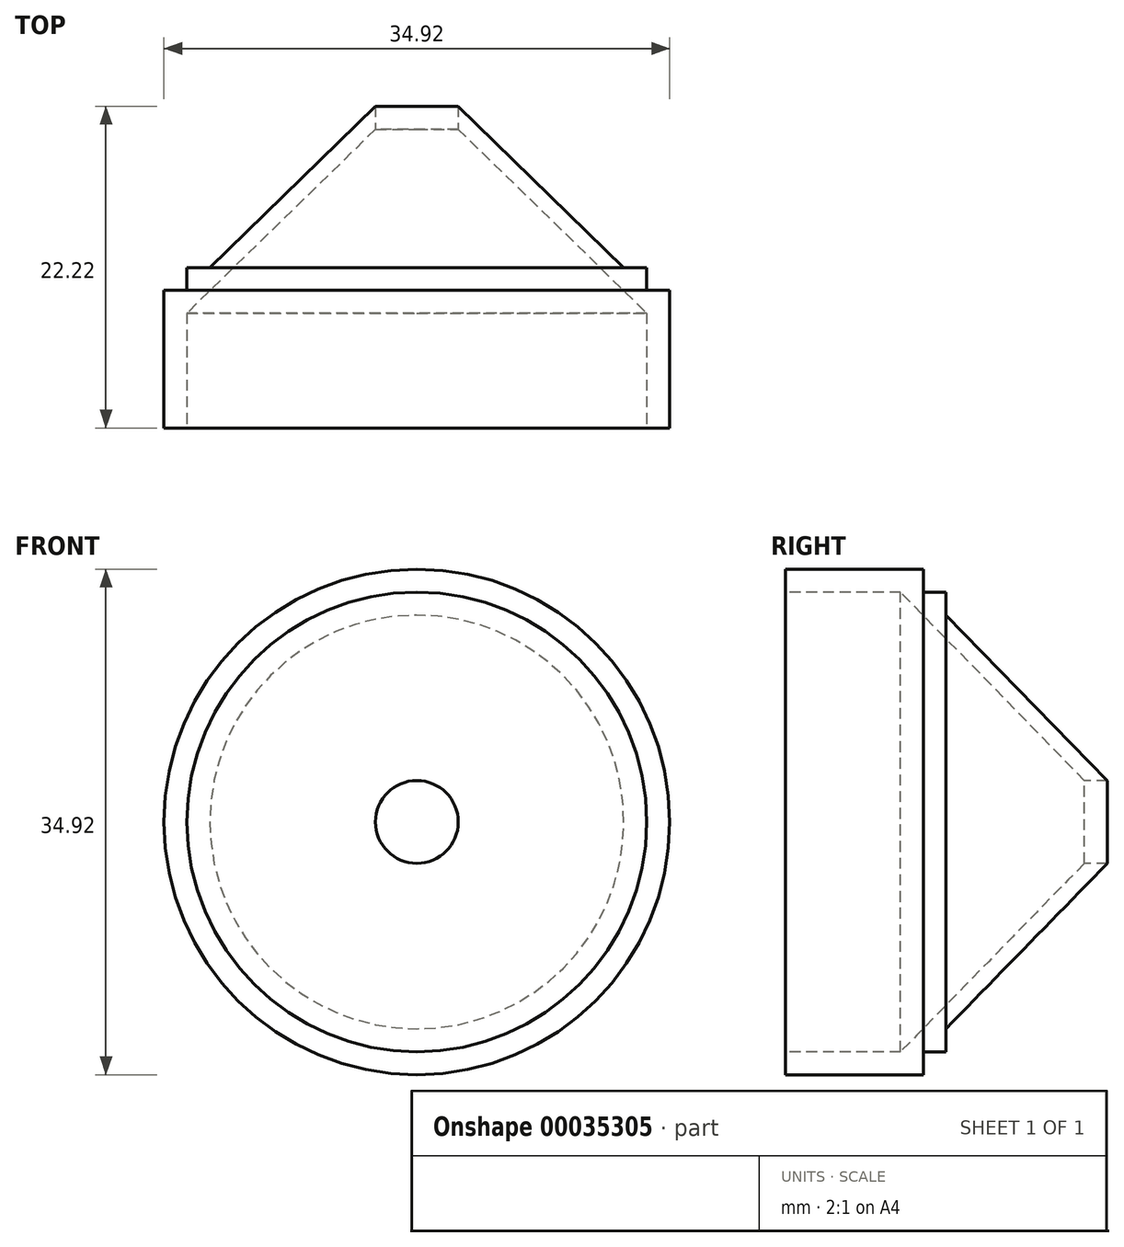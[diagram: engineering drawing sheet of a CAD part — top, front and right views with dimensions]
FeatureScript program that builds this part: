
annotation { "Feature Type Name" : "Feature", "Feature Type Description" : "" }
export const myFeature = defineFeature(function(context is Context, id is Id, definition is map)
    precondition{}
    {
        {
            var Q0;
            Q0=qCreatedBy(makeId("Right.planeOp"),FACE);
            var sketch = newSketch(context, id + "F0", { "sketchPlane" : qUnion([Q0])});
            skLineSegment(sketch, "E0", {"start": v(-7.7, 0) * mm, "end": v(25.51, 0) * mm, "construction": true});
            skLineSegment(sketch, "E1", {"start": v(-11.9, 15.88) * mm, "end": v(-11.9, 17.46) * mm});
            skLineSegment(sketch, "E2", {"start": v(-11.9, 17.46) * mm, "end": v(-21.43, 17.46) * mm});
            skLineSegment(sketch, "E3", {"start": v(-21.43, 17.46) * mm, "end": v(-21.43, 15.88) * mm});
            skLineSegment(sketch, "E4", {"start": v(-21.43, 15.88) * mm, "end": v(-13.5, 15.88) * mm});
            skLineSegment(sketch, "E5", {"start": v(-13.5, 15.88) * mm, "end": v(-0.8, 2.86) * mm});
            skLineSegment(sketch, "E6", {"start": v(-0.8, 2.86) * mm, "end": v(0.8, 2.86) * mm});
            skPoint(sketch, "E7", {"position": v(0, 2.86) * mm});
            skLineSegment(sketch, "E8", {"start": v(-11.9, 15.88) * mm, "end": v(-10.36, 15.88) * mm});
            skLineSegment(sketch, "E9", {"start": v(-10.36, 15.88) * mm, "end": v(-10.36, 14.29) * mm});
            skLineSegment(sketch, "E10", {"start": v(-10.36, 14.29) * mm, "end": v(0.8, 2.86) * mm});
            skSolve(sketch);
        }
        {
            var Q0;
            Q0=makeQuery(id+"F0.imprint","IMPRINT",FACE,{"disambiguationData":[TD([[makeQuery(id+"F0.imprint","IMPRINT",EDGE,{"derivedFrom":sQuery(id+"F0.wireOp",EDGE,"E1")}),1.0]])]});
            var Q1;
            Q1=sQuery(id+"F0.wireOp",EDGE,"E0");
            revolve(context, id + "F1", {"entities" : qUnion([Q0]), "axis" : qUnion([Q1]), "revolveType" : RevolveType.FULL});
        }
    });
